# Revit family: LAMP_ARO OPAL IP54
name_source: partatom
category: Modelos genéricos
revit_build: Autodesk Revit 2015 (Build: 20140606_1530(x64)
units: mm (PartAtom-declared; Revit-internal decimal feet)

## types (2) — shared parameters
Comentarios de tipo = Availability of switching between accessories through visibility parameters when placed in a project.
Diameter = 174 mm  [stored 0.570866 ft]
Fabricante = LAMP
Grosor aro = 3 mm  [stored 0.00984252 ft]
Luminaire type = Accessory
Manufacturer URL = http://www.lamp.es
Manufacturer country = Spain
Manufacturer name = LAMP
Model explanation = Availability of switching between accessories through visibility parameters when placed in a project.
Product datasheet = https://www.lamp.es
Protection rating = IP54
Weight = 0.22 kg

## per-type parameters (varying)
| type | Descripción | Finish | Last update | Material Aro | Material Cristal | Modelo | Product code |
| WHITE | DOMO 220 ACC.TRANSP GLASS WH. | Matt white | 29/06/2020 | LAMP_PC Kombic Aro BL | LAMP_PC Cristal opal aro Kombic | DIOPRD240W | DIOPRD240W |
| GREY | DOMO 220 ACC.TRANSP GLASS GR. | Gloss grey | 14/05/2018 | LAMP_PC Kombic Aro GR | LAMP_CRISTAL ARO | DITRRD240G | DITRRD240G |

note: [stored X ft] marks values corroborated as IEEE doubles in the binary element streams (Revit-internal decimal feet)
